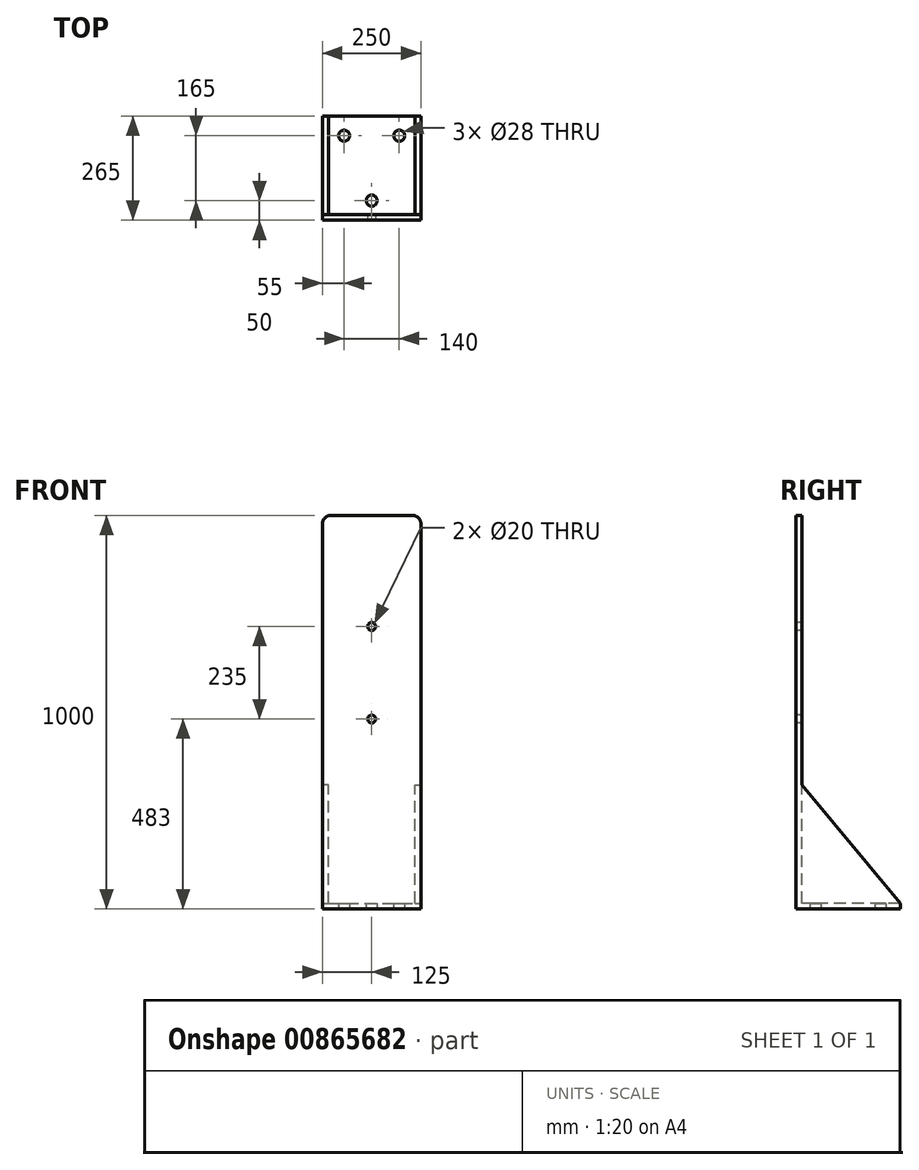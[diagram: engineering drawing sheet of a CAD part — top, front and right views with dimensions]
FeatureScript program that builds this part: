
annotation { "Feature Type Name" : "Feature", "Feature Type Description" : "" }
export const myFeature = defineFeature(function(context is Context, id is Id, definition is map)
    precondition{}
    {
        {
            var Q0;
            Q0=qCreatedBy(makeId("Front.planeOp"),FACE);
            var sketch = newSketch(context, id + "F0", { "sketchPlane" : qUnion([Q0])});
            skLineSegment(sketch, "E0.bottom", {"start": v(0, 0) * mm, "end": v(250, 0) * mm});
            skLineSegment(sketch, "E0.top", {"start": v(0, 1000) * mm, "end": v(250, 1000) * mm});
            skLineSegment(sketch, "E0.left", {"start": v(0, 0) * mm, "end": v(0, 1000) * mm});
            skLineSegment(sketch, "E0.right", {"start": v(250, 0) * mm, "end": v(250, 1000) * mm});
            skSolve(sketch);
        }
        {
            var Q0;
            Q0 = qSketchRegion(id + "F0", true);
            extrude(context, id + "F1", {"entities" : qUnion([Q0]), "depth" : 15 * mm, "offsetDistance" : 25 * mm});
        }
        {
            var Q0;
            Q0=makeQuery(id+"F1.opExtrude","SWEPT_EDGE",EDGE,{"disambiguationData":[OSD([sQuery(id+"F0.wireOp",EDGE,"E0.top"),sQuery(id+"F0.wireOp",EDGE,"E0.left")])]});
            fillet(context, id + "F2", {"entities" : qUnion([Q0]), "radius" : 20 * mm, "tangentPropagation" : true, "allowEdgeOverflow" : false});
        }
        {
            var Q0;
            Q0=makeQuery(id+"F1.opExtrude","SWEPT_EDGE",EDGE,{"disambiguationData":[OSD([sQuery(id+"F0.wireOp",EDGE,"E0.top"),sQuery(id+"F0.wireOp",EDGE,"E0.right")])]});
            fillet(context, id + "F3", {"entities" : qUnion([Q0]), "radius" : 20 * mm, "tangentPropagation" : true, "allowEdgeOverflow" : false});
        }
        {
            var Q0;
            Q0=makeQuery(id+"F1.opExtrude","CAP_FACE",FACE,{"disambiguationData":[OSD([sQuery(id+"F0.wireOp",EDGE,"E0.bottom"),sQuery(id+"F0.wireOp",EDGE,"E0.top"),sQuery(id+"F0.wireOp",EDGE,"E0.left"),sQuery(id+"F0.wireOp",EDGE,"E0.right")])],"isStart":true});
            var sketch = newSketch(context, id + "F4", { "sketchPlane" : qUnion([Q0])});
            skLineSegment(sketch, "E1.bottom", {"start": v(0, 0) * mm, "end": v(-250, 0) * mm});
            skLineSegment(sketch, "E1.top", {"start": v(0, 15) * mm, "end": v(-250, 15) * mm});
            skLineSegment(sketch, "E1.left", {"start": v(0, 0) * mm, "end": v(0, 15) * mm});
            skLineSegment(sketch, "E1.right", {"start": v(-250, 0) * mm, "end": v(-250, 15) * mm});
            skSolve(sketch);
        }
        {
            var Q0;
            Q0 = qSketchRegion(id + "F4", true);
            extrude(context, id + "F5", {"entities" : qUnion([Q0]), "operationType" : NewBodyOperationType.ADD, "depth" : 250 * mm, "offsetDistance" : 25 * mm});
        }
        {
            var Q0;
            Q0=makeQuery(id+"F5.boolean.opBoolean","MERGE",FACE,{"derivedFrom":[makeQuery(id+"F1.opExtrude","SWEPT_FACE",FACE,{"disambiguationData":[OSD([sQuery(id+"F0.wireOp",EDGE,"E0.left")])]}),makeQuery(id+"F5.opExtrude","SWEPT_FACE",FACE,{"disambiguationData":[OSD([sQuery(id+"F4.wireOp",EDGE,"E1.left")])]})]});
            var sketch = newSketch(context, id + "F6", { "sketchPlane" : qUnion([Q0])});
            skLineSegment(sketch, "E2", {"start": v(-250, 15) * mm, "end": v(0, 15) * mm});
            skLineSegment(sketch, "E3", {"start": v(0, 15) * mm, "end": v(0, 315) * mm});
            skLineSegment(sketch, "E4", {"start": v(0, 315) * mm, "end": v(-250, 15) * mm});
            skSolve(sketch);
        }
        {
            var Q0;
            Q0=makeQuery(id+"F6.imprint","IMPRINT",FACE,{"disambiguationData":[TD([[makeQuery(id+"F6.imprint","IMPRINT",EDGE,{"derivedFrom":sQuery(id+"F6.wireOp",EDGE,"E2")}),1.0]])]});
            extrude(context, id + "F7", {"entities" : qUnion([Q0]), "operationType" : NewBodyOperationType.ADD, "depth" : -15 * mm, "offsetDistance" : 25 * mm});
        }
        {
            var Q0;
            Q0=makeQuery(id+"F5.boolean.opBoolean","MERGE",FACE,{"derivedFrom":[makeQuery(id+"F1.opExtrude","SWEPT_FACE",FACE,{"disambiguationData":[OSD([sQuery(id+"F0.wireOp",EDGE,"E0.right")])]}),makeQuery(id+"F5.opExtrude","SWEPT_FACE",FACE,{"disambiguationData":[OSD([sQuery(id+"F4.wireOp",EDGE,"E1.right")])]})]});
            var sketch = newSketch(context, id + "F8", { "sketchPlane" : qUnion([Q0])});
            skLineSegment(sketch, "E5", {"start": v(250, 15) * mm, "end": v(0, 15) * mm});
            skLineSegment(sketch, "E6", {"start": v(0, 15) * mm, "end": v(0, 315) * mm});
            skLineSegment(sketch, "E7", {"start": v(0, 315) * mm, "end": v(250, 15) * mm});
            skSolve(sketch);
        }
        {
            var Q0;
            Q0=makeQuery(id+"F8.imprint","IMPRINT",FACE,{"disambiguationData":[TD([[makeQuery(id+"F8.imprint","IMPRINT",EDGE,{"derivedFrom":sQuery(id+"F8.wireOp",EDGE,"E5")}),-1.0]])]});
            extrude(context, id + "F9", {"entities" : qUnion([Q0]), "operationType" : NewBodyOperationType.ADD, "depth" : -15 * mm, "offsetDistance" : 25 * mm});
        }
        {
            var Q0;
            Q0=makeQuery(id+"F5.boolean.opBoolean","MERGE",FACE,{"derivedFrom":[makeQuery(id+"F1.opExtrude","SWEPT_FACE",FACE,{"disambiguationData":[OSD([sQuery(id+"F0.wireOp",EDGE,"E0.bottom")])]}),makeQuery(id+"F5.opExtrude","SWEPT_FACE",FACE,{"disambiguationData":[OSD([sQuery(id+"F4.wireOp",EDGE,"E1.bottom")])]})]});
            var sketch = newSketch(context, id + "F10", { "sketchPlane" : qUnion([Q0])});
            skCircle(sketch, "E8", {"center": v(125, -35) * mm, "radius": 14 * mm});
            skCircle(sketch, "E9", {"center": v(195, -200) * mm, "radius": 14 * mm});
            skLineSegment(sketch, "E10", {"start": v(125, -250) * mm, "end": v(125, 15) * mm, "construction": true});
            skLineSegment(sketch, "E11", {"start": v(0, -200) * mm, "end": v(250, -200) * mm, "construction": true});
            skCircle(sketch, "E12", {"center": v(55, -200) * mm, "radius": 14 * mm});
            skSolve(sketch);
        }
        {
            var Q0;
            Q0 = qSketchRegion(id + "F10", true);
            extrude(context, id + "F11", {"entities" : qUnion([Q0]), "operationType" : NewBodyOperationType.REMOVE, "depth" : -15 * mm, "offsetDistance" : 25 * mm});
        }
        {
            var Q0;
            Q0=makeQuery(id+"F1.opExtrude","CAP_FACE",FACE,{"disambiguationData":[OSD([sQuery(id+"F0.wireOp",EDGE,"E0.bottom"),sQuery(id+"F0.wireOp",EDGE,"E0.top"),sQuery(id+"F0.wireOp",EDGE,"E0.left"),sQuery(id+"F0.wireOp",EDGE,"E0.right")])],"isStart":false});
            var sketch = newSketch(context, id + "F12", { "sketchPlane" : qUnion([Q0])});
            skLineSegment(sketch, "E13", {"start": v(125, 1000) * mm, "end": v(125, 0) * mm, "construction": true});
            skCircle(sketch, "E14", {"center": v(125, 718) * mm, "radius": 10 * mm});
            skCircle(sketch, "E15", {"center": v(125, 483) * mm, "radius": 10 * mm});
            skSolve(sketch);
        }
        {
            var Q0;
            Q0 = qSketchRegion(id + "F12", true);
            extrude(context, id + "F13", {"entities" : qUnion([Q0]), "operationType" : NewBodyOperationType.REMOVE, "endBound" : BoundingType.THROUGH_ALL, "oppositeDirection" : true, "depth" : 25 * mm, "offsetDistance" : 25 * mm});
        }
    });
